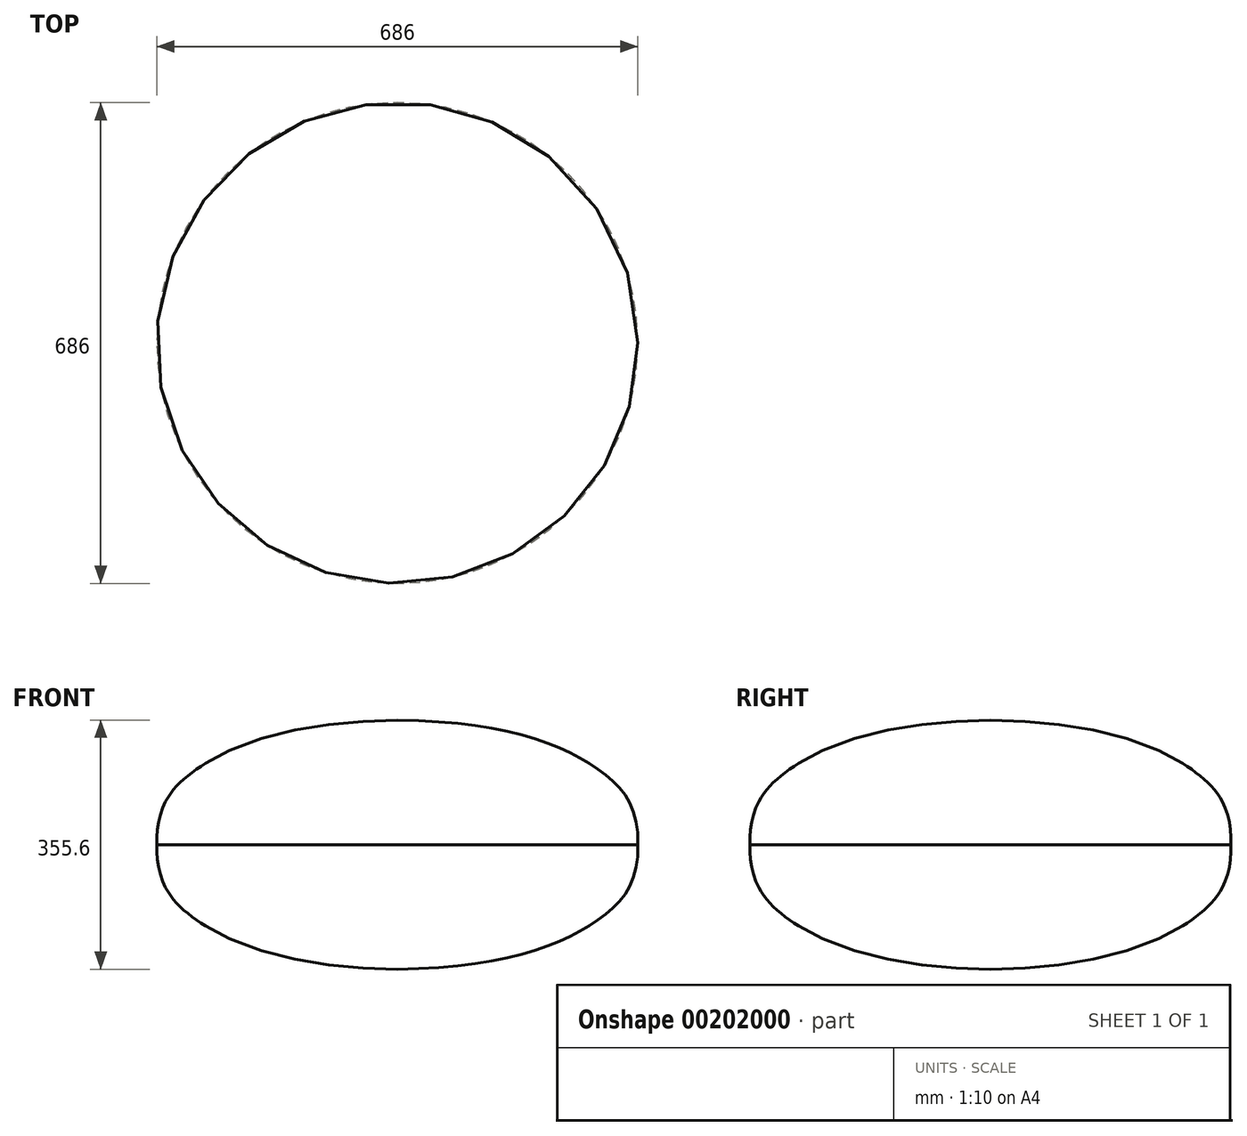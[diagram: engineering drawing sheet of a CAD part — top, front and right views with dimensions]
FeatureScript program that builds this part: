
annotation { "Feature Type Name" : "Feature", "Feature Type Description" : "" }
export const myFeature = defineFeature(function(context is Context, id is Id, definition is map)
    precondition{}
    {
        {
            var Q0;
            Q0=qCreatedBy(makeId("Front.planeOp"),FACE);
            var sketch = newSketch(context, id + "F0", { "sketchPlane" : qUnion([Q0])});
            skLineSegment(sketch, "E0", {"start": v(0, 0) * mm, "end": v(342.9, 0) * mm, "construction": true});
            skLineSegment(sketch, "E1", {"start": v(0, 0) * mm, "end": v(0, 177.8) * mm, "construction": true});
            skFitSpline(sketch, "E2", {"points": [v(0, 177.8) * mm, v(285.76, 107.95) * mm, v(342.9, 0) * mm], "startDerivative": vector(724.14, -10.85) * mm, "endDerivative": vector(-13.78, -419.29) * mm});
            skFitSpline(sketch, "E3.MirrorCS", {"points": [v(0, -177.8) * mm, v(285.76, -107.95) * mm, v(342.9, 0) * mm], "startDerivative": vector(724.14, 10.85) * mm, "endDerivative": vector(-13.78, 419.29) * mm});
            skLineSegment(sketch, "E4", {"start": v(0, 177.8) * mm, "end": v(0, -177.8) * mm});
            skSolve(sketch);
        }
        {
            var Q0;
            Q0=makeQuery(id+"F0.imprint","IMPRINT",FACE,{"disambiguationData":[TD([[makeQuery(id+"F0.imprint","IMPRINT",EDGE,{"derivedFrom":sQuery(id+"F0.wireOp",EDGE,"E2")}),-1.0]])]});
            var Q1;
            Q1=sQuery(id+"F0.wireOp",EDGE,"E4");
            var Q2;
            Q2=sQuery(id+"F0.wireOp",EDGE,"E2");
            var Q3;
            Q3=sQuery(id+"F0.wireOp",EDGE,"E3.MirrorCS");
            var Q4;
            Q4=sQuery(id+"F0.wireOp",EDGE,"E4");
            revolve(context, id + "F1", {"entities" : qUnion([Q0]), "surfaceEntities" : qUnion([Q1, Q2, Q3]), "axis" : qUnion([Q4]), "revolveType" : RevolveType.FULL});
        }
    });
